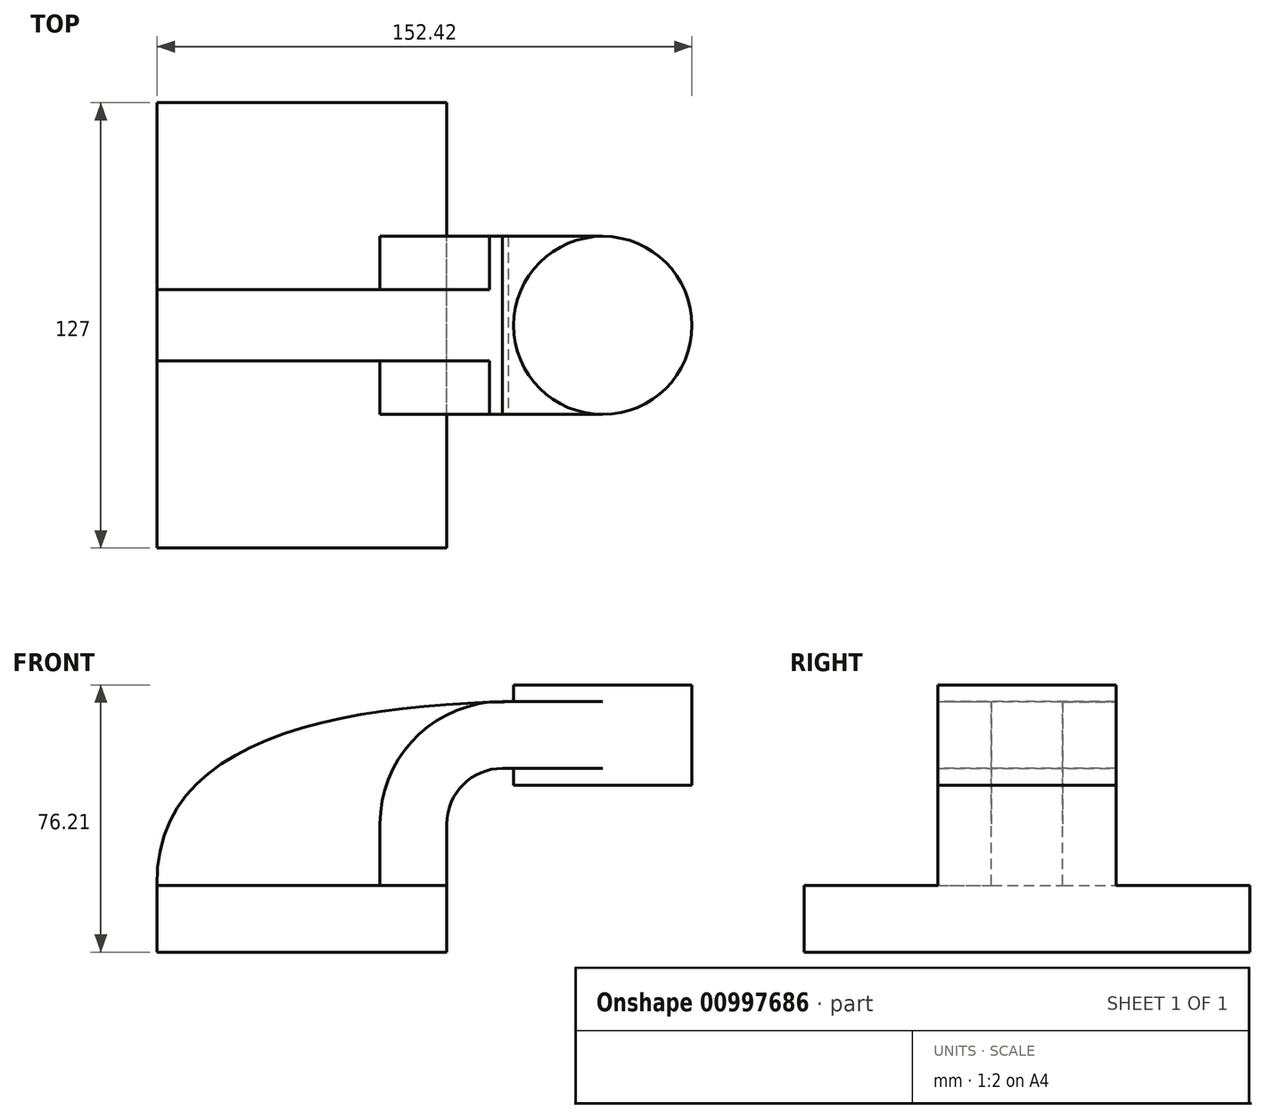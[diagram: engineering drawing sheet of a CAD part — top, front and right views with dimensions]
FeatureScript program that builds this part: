
annotation { "Feature Type Name" : "Feature", "Feature Type Description" : "" }
export const myFeature = defineFeature(function(context is Context, id is Id, definition is map)
    precondition{}
    {
        {
            var Q0;
            Q0=qCreatedBy(makeId("Front.planeOp"),FACE);
            var sketch = newSketch(context, id + "F0", { "sketchPlane" : qUnion([Q0])});
            skLineSegment(sketch, "E0.bottom", {"start": v(-41.28, 9.53) * mm, "end": v(41.28, 9.53) * mm});
            skLineSegment(sketch, "E0.top", {"start": v(-41.28, -9.53) * mm, "end": v(41.28, -9.53) * mm});
            skLineSegment(sketch, "E0.left", {"start": v(-41.28, 9.53) * mm, "end": v(-41.28, -9.53) * mm});
            skLineSegment(sketch, "E0.right", {"start": v(41.28, 9.53) * mm, "end": v(41.28, -9.53) * mm});
            skPoint(sketch, "E0.middle", {"position": v(0, 0) * mm});
            skLineSegment(sketch, "E1.bottom", {"start": v(60.33, 38.1) * mm, "end": v(111.13, 38.1) * mm});
            skLineSegment(sketch, "E1.top", {"start": v(60.33, 66.67) * mm, "end": v(111.12, 66.67) * mm});
            skLineSegment(sketch, "E1.left", {"start": v(60.33, 38.1) * mm, "end": v(60.33, 66.67) * mm});
            skLineSegment(sketch, "E1.right", {"start": v(111.12, 38.1) * mm, "end": v(111.12, 66.68) * mm});
            skPoint(sketch, "E1.middle", {"position": v(85.73, 52.39) * mm});
            skLineSegment(sketch, "E2", {"start": v(41.28, 9.53) * mm, "end": v(41.28, 27) * mm});
            skArc(sketch, "E3", {"start": v(41.28, 27) * mm, "mid": v(45.92, 38.23) * mm, "end": v(57.15, 42.88) * mm});
            skLineSegment(sketch, "E4", {"start": v(57.15, 42.88) * mm, "end": v(85.72, 42.88) * mm});
            skArc(sketch, "E5.0", {"start": v(22.23, 27) * mm, "mid": v(33.05, 52.28) * mm, "end": v(58.82, 61.89) * mm});
            skLineSegment(sketch, "E6.0", {"start": v(22.23, 9.53) * mm, "end": v(22.23, 27) * mm});
            skLineSegment(sketch, "E7.0", {"start": v(57.15, 61.93) * mm, "end": v(85.72, 61.93) * mm});
            skLineSegment(sketch, "E8", {"start": v(85.72, 66.67) * mm, "end": v(85.72, 38.1) * mm});
            skFitSpline(sketch, "E9", {"points": [v(-41.28, 9.53) * mm, v(58.82, 61.89) * mm], "startDerivative": vector(-3.27, 123.97) * mm, "endDerivative": vector(149.88, 3.32) * mm});
            skSolve(sketch);
        }
        {
            var Q0;
            Q0=makeQuery(id+"F0.imprint","IMPRINT",FACE,{"disambiguationData":[TD([[makeQuery(id+"F0.imprint","IMPRINT",EDGE,{"derivedFrom":sQuery(id+"F0.wireOp",EDGE,"E0.top")}),1.0]])]});
            extrude(context, id + "F1", {"entities" : qUnion([Q0]), "endBound" : BoundingType.SYMMETRIC, "depth" : 127 * mm, "offsetDistance" : 25.4 * mm});
        }
        {
            var Q0;
            {var subQ0=sQuery(id+"F0.wireOp",EDGE,"E4");var subQ1=sQuery(id+"F0.wireOp",EDGE,"E1.left");var subQ2=makeQuery(id+"F0.imprint","INTERSECT",VERTEX,{"derivedFrom":[subQ1,subQ0]});Q0=makeQuery(id+"F0.imprint","IMPRINT",FACE,{"disambiguationData":[TD([[makeQuery(id+"F0.imprint","IMPRINT",EDGE,{"disambiguationData":[TD([[subQ2,-1.0]])],"derivedFrom":subQ1}),-1.0]])]});}
            var Q1;
            {var subQ1=sQuery(id+"F0.wireOp",EDGE,"E2");Q1=makeQuery(id+"F0.imprint","IMPRINT",FACE,{"disambiguationData":[TD([[makeQuery(id+"F0.imprint","IMPRINT",EDGE,{"derivedFrom":subQ1}),1.0]])]});}
            extrude(context, id + "F2", {"entities" : qUnion([Q0, Q1]), "operationType" : NewBodyOperationType.ADD, "endBound" : BoundingType.SYMMETRIC, "depth" : 50.8 * mm, "offsetDistance" : 25.4 * mm});
        }
        {
            var Q0;
            {var subQ0=sQuery(id+"F0.wireOp",EDGE,"E1.right");Q0=makeQuery(id+"F0.imprint","IMPRINT",FACE,{"disambiguationData":[TD([[makeQuery(id+"F0.imprint","IMPRINT",EDGE,{"derivedFrom":subQ0}),1.0]])]});}
            var Q1;
            Q1=sQuery(id+"F0.wireOp",EDGE,"E8");
            revolve(context, id + "F3", {"operationType" : NewBodyOperationType.ADD, "surfaceOperationType" : NewSurfaceOperationType.NEW, "entities" : qUnion([Q0]), "axis" : qUnion([Q1]), "revolveType" : RevolveType.FULL});
        }
        {
            var Q0;
            {var subQ3=sQuery(id+"F0.wireOp",EDGE,"E6.0");Q0=makeQuery(id+"F0.imprint","IMPRINT",FACE,{"disambiguationData":[TD([[makeQuery(id+"F0.imprint","IMPRINT",EDGE,{"derivedFrom":subQ3}),1.0]])]});}
            extrude(context, id + "F4", {"entities" : qUnion([Q0]), "operationType" : NewBodyOperationType.ADD, "endBound" : BoundingType.SYMMETRIC, "depth" : 20.32 * mm, "offsetDistance" : 25.4 * mm});
        }
    });
